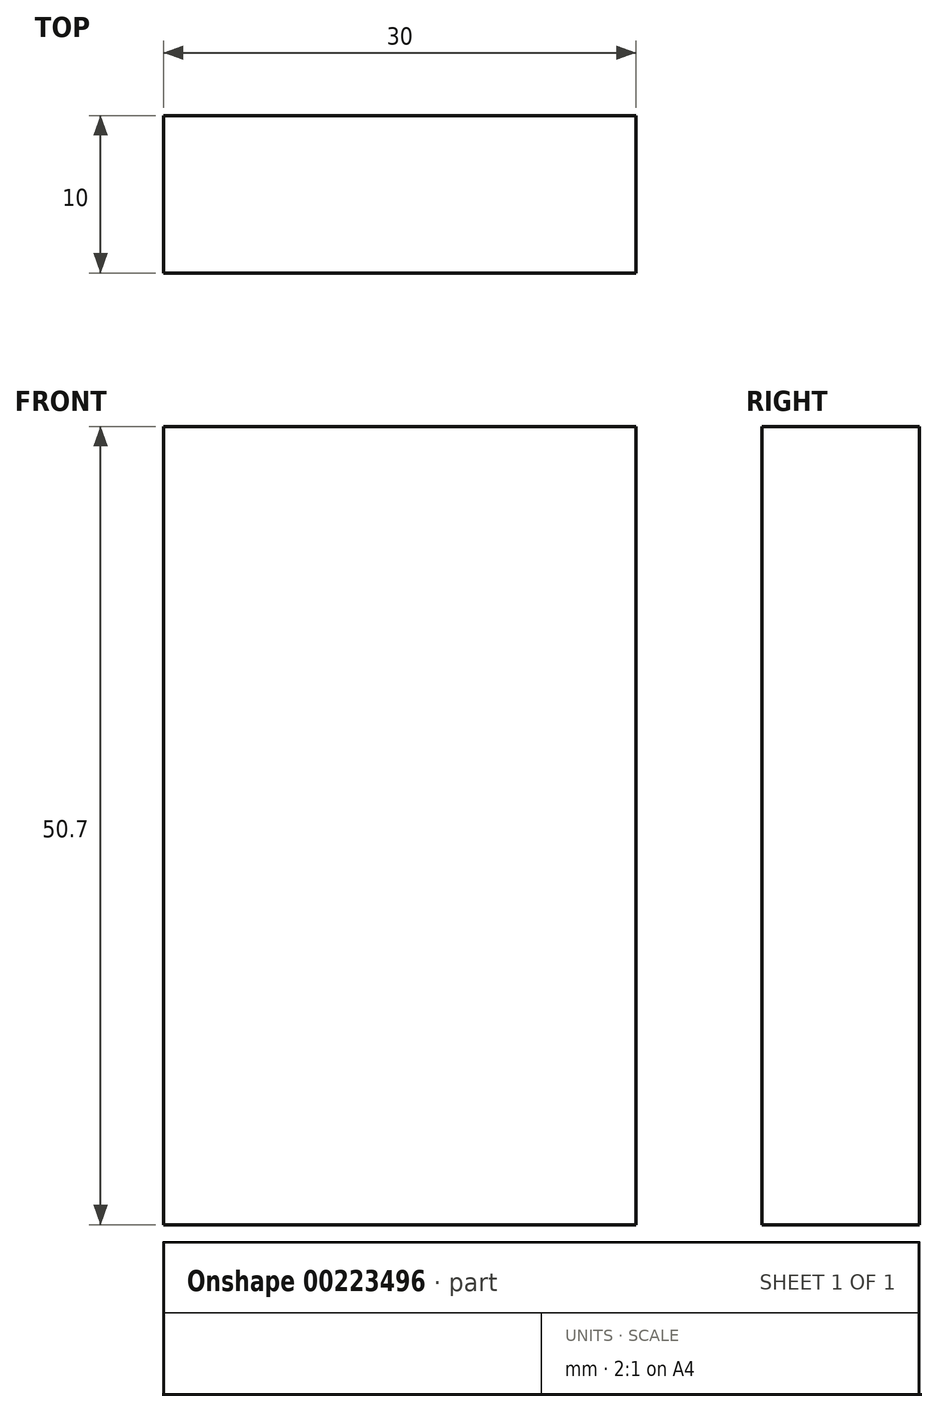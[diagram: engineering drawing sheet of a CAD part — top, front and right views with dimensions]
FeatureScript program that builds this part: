
annotation { "Feature Type Name" : "Feature", "Feature Type Description" : "" }
export const myFeature = defineFeature(function(context is Context, id is Id, definition is map)
    precondition{}
    {
        {
            var Q0;
            Q0=qCreatedBy(makeId("Top.planeOp"),FACE);
            var sketch = newSketch(context, id + "F0", { "sketchPlane" : qUnion([Q0])});
            skLineSegment(sketch, "E0.bottom", {"start": v(0, 0) * mm, "end": v(0, -10) * mm});
            skLineSegment(sketch, "E0.top", {"start": v(30, 0) * mm, "end": v(30, -10) * mm});
            skLineSegment(sketch, "E0.left", {"start": v(0, 0) * mm, "end": v(30, 0) * mm});
            skLineSegment(sketch, "E0.right", {"start": v(0, -10) * mm, "end": v(30, -10) * mm});
            skSolve(sketch);
        }
        {
            var Q0;
            Q0 = qSketchRegion(id + "F0", true);
            extrude(context, id + "F1", {"entities" : qUnion([Q0]), "depth" : 50.7 * mm});
        }
    });
